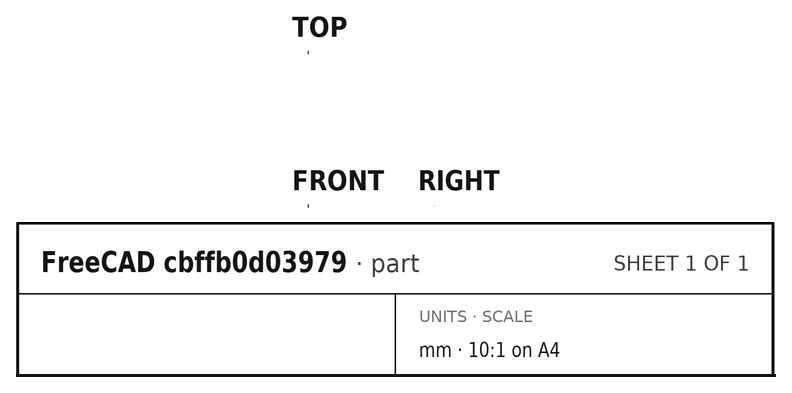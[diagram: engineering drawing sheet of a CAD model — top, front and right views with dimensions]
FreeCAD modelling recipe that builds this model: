
FCSTD DOCUMENT  (FreeCAD 0.21R33694 (Git))
Label: Lee_microstrip
License: All rights reserved
LicenseURL: http://en.wikipedia.org/wiki/All_rights_reserved
objects: Part::Part2DObjectPython×4, Part::Cut×1, Part::FeaturePython×1, App::FeaturePython×1
note: 6 computed .brp shape members not serialized (recipe doc carries the construction recipe); baked Part::Feature solids carry a one-line shape summary decoded from their .brp

FEATURE [Part::Part2DObjectPython] Line  label="_PV1"  # Draft 2D object (typed FeaturePython)
  Area = 0
  ChamferSize = 0
  Closed = false
  End = (0.00125,0.00025,0)
  FilletRadius = 0
  Length = 0.00025
  MakeFace = true
  Placement = pos=(0.0025,0,0) rot=(0,0,1;0rad)
  Points = (2) [(-0.00125,3.82702e-20,0),(-0.00125,0.00025,0)]
  Start = (0.00125,0,0)
  Subdivisions = 0
FEATURE [Part::Part2DObjectPython] Rectangle004  label="Lee_semiconductor"  # Draft 2D object (typed FeaturePython)
  Area = 6.25e-07
  ChamferSize = 0
  Columns = 1
  FilletRadius = 0
  Height = 0.00025
  Length = 0.0025
  MakeFace = true
  Rows = 1
FEATURE [Part::Part2DObjectPython] Rectangle005  label="strip001"  # Draft 2D object (typed FeaturePython)
  Area = 1.25e-08
  ChamferSize = 0
  Columns = 1
  FilletRadius = 0
  Height = 5e-05
  Length = 0.00025
  MakeFace = true
  Placement = pos=(0.001125,0.00025,0) rot=(0,0,1;0rad)
  Rows = 1
FEATURE [Part::Part2DObjectPython] Rectangle006  label="air001"  # Draft 2D object (typed FeaturePython)
  Area = 5.625e-06
  ChamferSize = 0
  Columns = 1
  FilletRadius = 0
  Height = 0.00225
  Length = 0.0025
  MakeFace = true
  Placement = pos=(0,0.00025,0) rot=(0,0,1;0rad)
  Rows = 1
FEATURE [Part::Cut] Cut001  label="air002"
  Base = -> Rectangle006
  Tool = -> Rectangle005
FEATURE [Part::FeaturePython] BooleanFragments001  label="Lee_microstrip"  # WARN: FeaturePython — macro-defined, semantics opaque (R4)
  Mode = 0
  Objects = -> [Rectangle004,Cut001]
  Tolerance = 0
FEATURE [App::FeaturePython] Text  label="_L1(voltage){V1}"  # WARN: FeaturePython — macro-defined, semantics opaque (R4)
  Placement = pos=(0.00123975,-0.000526531,0) rot=(0,0,1;0rad)
  Text = .
